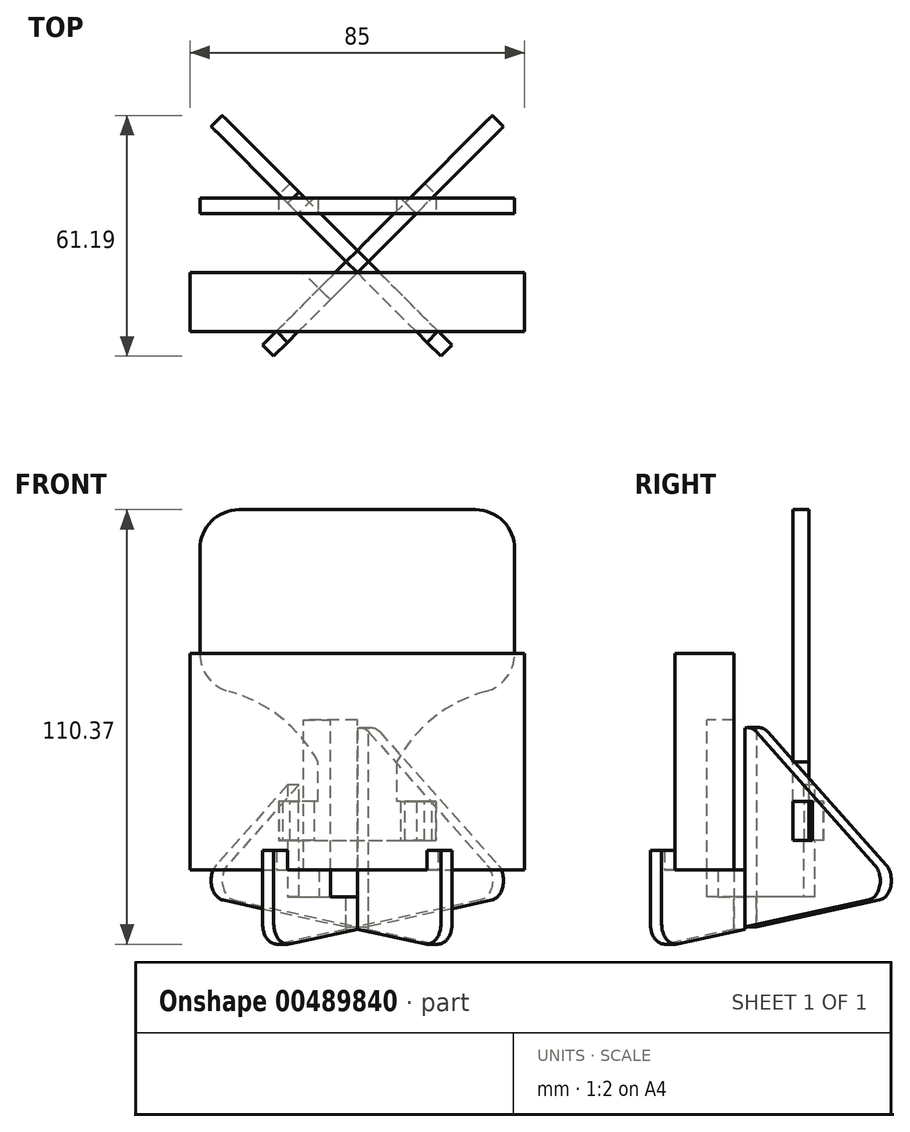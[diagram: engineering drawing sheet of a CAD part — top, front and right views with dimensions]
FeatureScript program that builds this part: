
annotation { "Feature Type Name" : "Feature", "Feature Type Description" : "" }
export const myFeature = defineFeature(function(context is Context, id is Id, definition is map)
    precondition{}
    {
        {
            var Q0;
            Q0=qCreatedBy(makeId("Front.planeOp"),FACE);
            var sketch = newSketch(context, id + "F0", { "sketchPlane" : qUnion([Q0])});
            skLineSegment(sketch, "E0.bottom", {"start": v(-42.5, 27.5) * mm, "end": v(42.5, 27.5) * mm});
            skLineSegment(sketch, "E0.top", {"start": v(-42.5, -27.5) * mm, "end": v(42.5, -27.5) * mm});
            skLineSegment(sketch, "E0.left", {"start": v(-42.5, 27.5) * mm, "end": v(-42.5, -27.5) * mm});
            skLineSegment(sketch, "E0.right", {"start": v(42.5, 27.5) * mm, "end": v(42.5, -27.5) * mm});
            skPoint(sketch, "E0.middle", {"position": v(0, 0) * mm});
            skSolve(sketch);
        }
        {
            var Q0;
            Q0=makeQuery(id+"F0.imprint","IMPRINT",FACE,{"disambiguationData":[TD([[makeQuery(id+"F0.imprint","IMPRINT",EDGE,{"derivedFrom":sQuery(id+"F0.wireOp",EDGE,"E0.bottom")}),-1.0]])]});
            extrude(context, id + "F1", {"entities" : qUnion([Q0]), "depth" : 15 * mm});
        }
        {
            var Q0;
            Q0=makeQuery(id+"F1.opExtrude","CAP_FACE",FACE,{"disambiguationData":[OSD([sQuery(id+"F0.wireOp",EDGE,"E0.bottom"),sQuery(id+"F0.wireOp",EDGE,"E0.top"),sQuery(id+"F0.wireOp",EDGE,"E0.left"),sQuery(id+"F0.wireOp",EDGE,"E0.right")])],"isStart":true});
            var sketch = newSketch(context, id + "F2", { "sketchPlane" : qUnion([Q0])});
            skLineSegment(sketch, "E1", {"start": v(0, -27.5) * mm, "end": v(0, 27.5) * mm});
            skSolve(sketch);
        }
        {
            var Q0;
            Q0=qCreatedBy(makeId("Front.planeOp"),FACE);
            var Q1;
            Q1=sQuery(id+"F2.wireOp",EDGE,"E1");
            cPlane(context, id + "F3", {"entities" : qUnion([Q0, Q1]), "cplaneType" : CPlaneType.LINE_ANGLE, "offset" : 25 * mm, "angle" : 45 * degree, "width" : 150 * mm, "height" : 150 * mm});
        }
        {
            var Q0;
            Q0=qCreatedBy(id+"F3.planeOp",FACE);
            var sketch = newSketch(context, id + "F4", { "sketchPlane" : qUnion([Q0])});
            skLineSegment(sketch, "E2", {"start": v(0, -27.5) * mm, "end": v(0, 3.7) * mm});
            skLineSegment(sketch, "E3", {"start": v(-8.11, 7.62) * mm, "end": v(-50.65, -26.24) * mm});
            skLineSegment(sketch, "E4", {"start": v(-48.3, -35.1) * mm, "end": v(24.24, -46.24) * mm});
            skLineSegment(sketch, "E5", {"start": v(30, -22.5) * mm, "end": v(25, -22.5) * mm});
            skLineSegment(sketch, "E6", {"start": v(25, -22.5) * mm, "end": v(25, -27.5) * mm});
            skLineSegment(sketch, "E7", {"start": v(25, -27.5) * mm, "end": v(0, -27.5) * mm});
            skLineSegment(sketch, "E8", {"start": v(30, -22.5) * mm, "end": v(30, -41.3) * mm});
            skPoint(sketch, "E9.visualSharp", {"position": v(0, 14.08) * mm});
            skArc(sketch, "E9.filletArc", {"start": v(0, 3.7) * mm, "mid": v(-2.83, 8.21) * mm, "end": v(-8.11, 7.62) * mm});
            skPoint(sketch, "E10.visualSharp", {"position": v(-59.6, -33.35) * mm});
            skArc(sketch, "E10.filletArc", {"start": v(-50.65, -26.24) * mm, "mid": v(-52.37, -31.43) * mm, "end": v(-48.3, -35.1) * mm});
            skPoint(sketch, "E11.visualSharp", {"position": v(30, -47.13) * mm});
            skArc(sketch, "E11.filletArc", {"start": v(24.24, -46.24) * mm, "mid": v(28.26, -45.1) * mm, "end": v(30, -41.3) * mm});
            skSolve(sketch);
        }
        {
            var Q0;
            Q0=makeQuery(id+"F4.imprint","IMPRINT",FACE,{"disambiguationData":[TD([[makeQuery(id+"F4.imprint","IMPRINT",EDGE,{"derivedFrom":sQuery(id+"F4.wireOp",EDGE,"E2")}),1.0]])]});
            extrude(context, id + "F5", {"entities" : qUnion([Q0]), "depth" : 4 * mm});
        }
        {
            var Q0;
            Q0=makeQuery(id+"F5.opExtrude","SWEPT_BODY",BODY,{"disambiguationData":[OSD([sQuery(id+"F4.wireOp",EDGE,"E2"),sQuery(id+"F4.wireOp",EDGE,"E3"),sQuery(id+"F4.wireOp",EDGE,"E4"),sQuery(id+"F4.wireOp",EDGE,"E5"),sQuery(id+"F4.wireOp",EDGE,"E6"),sQuery(id+"F4.wireOp",EDGE,"E7"),sQuery(id+"F4.wireOp",EDGE,"E8"),sQuery(id+"F4.wireOp",EDGE,"E9.filletArc"),sQuery(id+"F4.wireOp",EDGE,"E10.filletArc"),sQuery(id+"F4.wireOp",EDGE,"E11.filletArc")])]});
            var Q1;
            Q1=qCreatedBy(makeId("Right.planeOp"),FACE);
            mirror(context, id + "F6", {"entities" : qUnion([Q0]), "mirrorPlane" : qUnion([Q1])});
        }
        {
            var Q0;
            Q0=makeQuery(id+"F5.opExtrude","CAP_FACE",FACE,{"disambiguationData":[OSD([sQuery(id+"F4.wireOp",EDGE,"E2"),sQuery(id+"F4.wireOp",EDGE,"E3"),sQuery(id+"F4.wireOp",EDGE,"E4"),sQuery(id+"F4.wireOp",EDGE,"E5"),sQuery(id+"F4.wireOp",EDGE,"E6"),sQuery(id+"F4.wireOp",EDGE,"E7"),sQuery(id+"F4.wireOp",EDGE,"E8"),sQuery(id+"F4.wireOp",EDGE,"E9.filletArc"),sQuery(id+"F4.wireOp",EDGE,"E10.filletArc"),sQuery(id+"F4.wireOp",EDGE,"E11.filletArc")])],"isStart":true});
            var sketch = newSketch(context, id + "F7", { "sketchPlane" : qUnion([Q0])});
            skLineSegment(sketch, "E12.bottom", {"start": v(4, -34.3) * mm, "end": v(-9.7, -34.3) * mm});
            skLineSegment(sketch, "E12.top", {"start": v(4, 10.7) * mm, "end": v(-9.7, 10.7) * mm});
            skLineSegment(sketch, "E12.left", {"start": v(4, -34.3) * mm, "end": v(4, 10.7) * mm});
            skLineSegment(sketch, "E12.right", {"start": v(-9.7, -34.3) * mm, "end": v(-9.7, 10.7) * mm});
            skSolve(sketch);
        }
        {
            var Q0;
            Q0 = qSketchRegion(id + "F7", true);
            extrude(context, id + "F8", {"entities" : qUnion([Q0]), "operationType" : NewBodyOperationType.REMOVE, "oppositeDirection" : true, "depth" : 25 * mm});
        }
        {
            var Q0;
            Q0=makeQuery(id+"F6.opPattern","COPY",FACE,{"derivedFrom":makeQuery(id+"F5.opExtrude","CAP_FACE",FACE,{"disambiguationData":[OSD([sQuery(id+"F4.wireOp",EDGE,"E2"),sQuery(id+"F4.wireOp",EDGE,"E3"),sQuery(id+"F4.wireOp",EDGE,"E4"),sQuery(id+"F4.wireOp",EDGE,"E5"),sQuery(id+"F4.wireOp",EDGE,"E6"),sQuery(id+"F4.wireOp",EDGE,"E7"),sQuery(id+"F4.wireOp",EDGE,"E8"),sQuery(id+"F4.wireOp",EDGE,"E9.filletArc"),sQuery(id+"F4.wireOp",EDGE,"E10.filletArc"),sQuery(id+"F4.wireOp",EDGE,"E11.filletArc")])],"isStart":false}),"instanceName":"1"});
            var sketch = newSketch(context, id + "F9", { "sketchPlane" : qUnion([Q0])});
            skLineSegment(sketch, "E13.bottom", {"start": v(0, -50.3) * mm, "end": v(4, -50.3) * mm});
            skLineSegment(sketch, "E13.top", {"start": v(0, -48.84) * mm, "end": v(4, -48.84) * mm});
            skLineSegment(sketch, "E13.left", {"start": v(0, -48.84) * mm, "end": v(0, -50.3) * mm});
            skLineSegment(sketch, "E13.right", {"start": v(4, -48.84) * mm, "end": v(4, -50.3) * mm});
            skSolve(sketch);
        }
        {
            var Q0;
            Q0 = qSketchRegion(id + "F9", true);
            extrude(context, id + "F10", {"entities" : qUnion([Q0]), "operationType" : NewBodyOperationType.REMOVE, "oppositeDirection" : true, "depth" : 25 * mm});
        }
        {
            var Q0;
            Q0=makeQuery(id+"F6.opPattern","COPY",FACE,{"derivedFrom":makeQuery(id+"F5.opExtrude","CAP_FACE",FACE,{"disambiguationData":[OSD([sQuery(id+"F4.wireOp",EDGE,"E2"),sQuery(id+"F4.wireOp",EDGE,"E3"),sQuery(id+"F4.wireOp",EDGE,"E4"),sQuery(id+"F4.wireOp",EDGE,"E5"),sQuery(id+"F4.wireOp",EDGE,"E6"),sQuery(id+"F4.wireOp",EDGE,"E7"),sQuery(id+"F4.wireOp",EDGE,"E8"),sQuery(id+"F4.wireOp",EDGE,"E9.filletArc"),sQuery(id+"F4.wireOp",EDGE,"E10.filletArc"),sQuery(id+"F4.wireOp",EDGE,"E11.filletArc")])],"isStart":true}),"instanceName":"1"});
            var sketch = newSketch(context, id + "F11", { "sketchPlane" : qUnion([Q0])});
            skLineSegment(sketch, "E14.bottom", {"start": v(-4, -46.51) * mm, "end": v(0, -46.51) * mm});
            skLineSegment(sketch, "E14.top", {"start": v(-4, -34.3) * mm, "end": v(0, -34.3) * mm});
            skLineSegment(sketch, "E14.left", {"start": v(-4, -46.51) * mm, "end": v(-4, -34.3) * mm});
            skLineSegment(sketch, "E14.right", {"start": v(0, -46.51) * mm, "end": v(0, -34.3) * mm});
            skSolve(sketch);
        }
        {
            var Q0;
            Q0 = qSketchRegion(id + "F11", true);
            extrude(context, id + "F12", {"entities" : qUnion([Q0]), "operationType" : NewBodyOperationType.REMOVE, "oppositeDirection" : true, "depth" : 4 * mm});
        }
        {
            var Q0;
            Q0=qCreatedBy(makeId("Front.planeOp"),FACE);
            cPlane(context, id + "F13", {"entities" : qUnion([Q0]), "cplaneType" : CPlaneType.OFFSET, "offset" : 15 * mm, "oppositeDirection" : true, "width" : 150 * mm, "height" : 150 * mm});
        }
        {
            var Q0;
            Q0=qCreatedBy(id+"F13.planeOp",FACE);
            var sketch = newSketch(context, id + "F14", { "sketchPlane" : qUnion([Q0])});
            skLineSegment(sketch, "E15.bottom", {"start": v(-40, 64.07) * mm, "end": v(40, 64.07) * mm});
            skLineSegment(sketch, "E15.left", {"start": v(-40, 64.07) * mm, "end": v(-40, 19.07) * mm});
            skLineSegment(sketch, "E15.right", {"start": v(40, 64.07) * mm, "end": v(40, 19.07) * mm});
            skPoint(sketch, "E15.middle", {"position": v(0, 41.57) * mm});
            skArc(sketch, "E16", {"start": v(-10, 0) * mm, "mid": v(-22.5, 13.45) * mm, "end": v(-40, 19.07) * mm});
            skArc(sketch, "E17.MirrorCS", {"start": v(10, 0) * mm, "mid": v(22.5, 13.45) * mm, "end": v(40, 19.07) * mm});
            skLineSegment(sketch, "E18", {"start": v(10, 0) * mm, "end": v(10, -10) * mm});
            skLineSegment(sketch, "E19", {"start": v(10, -20) * mm, "end": v(-10, -20) * mm});
            skLineSegment(sketch, "E20", {"start": v(-10, -10) * mm, "end": v(-10, 0) * mm});
            skLineSegment(sketch, "E21", {"start": v(10, -20) * mm, "end": v(20, -20) * mm});
            skLineSegment(sketch, "E22", {"start": v(20, -20) * mm, "end": v(20, -10) * mm});
            skLineSegment(sketch, "E23", {"start": v(20, -10) * mm, "end": v(10, -10) * mm});
            skLineSegment(sketch, "E24", {"start": v(-20, -10) * mm, "end": v(-20, -20) * mm});
            skLineSegment(sketch, "E25", {"start": v(-20, -20) * mm, "end": v(-10, -20) * mm});
            skLineSegment(sketch, "E26.trimOffspring", {"start": v(-10, -10) * mm, "end": v(-20, -10) * mm});
            skSolve(sketch);
        }
        {
            var Q0;
            Q0 = qSketchRegion(id + "F14", true);
            extrude(context, id + "F15", {"entities" : qUnion([Q0]), "oppositeDirection" : true, "depth" : 4 * mm});
        }
        {
            var Q0;
            Q0=makeQuery(id+"F6.opPattern","COPY",FACE,{"derivedFrom":makeQuery(id+"F5.opExtrude","CAP_FACE",FACE,{"disambiguationData":[OSD([sQuery(id+"F4.wireOp",EDGE,"E2"),sQuery(id+"F4.wireOp",EDGE,"E3"),sQuery(id+"F4.wireOp",EDGE,"E4"),sQuery(id+"F4.wireOp",EDGE,"E5"),sQuery(id+"F4.wireOp",EDGE,"E6"),sQuery(id+"F4.wireOp",EDGE,"E7"),sQuery(id+"F4.wireOp",EDGE,"E8"),sQuery(id+"F4.wireOp",EDGE,"E9.filletArc"),sQuery(id+"F4.wireOp",EDGE,"E10.filletArc"),sQuery(id+"F4.wireOp",EDGE,"E11.filletArc")])],"isStart":true}),"instanceName":"1"});
            var sketch = newSketch(context, id + "F16", { "sketchPlane" : qUnion([Q0])});
            skLineSegment(sketch, "E27.bottom", {"start": v(-21.21, -10) * mm, "end": v(-28.08, -10) * mm});
            skLineSegment(sketch, "E27.top", {"start": v(-21.21, -20) * mm, "end": v(-28.08, -20) * mm});
            skLineSegment(sketch, "E27.left", {"start": v(-21.21, -10) * mm, "end": v(-21.21, -20) * mm});
            skLineSegment(sketch, "E27.right", {"start": v(-28.08, -10) * mm, "end": v(-28.08, -20) * mm});
            skSolve(sketch);
        }
        {
            var Q0;
            Q0 = qSketchRegion(id + "F16", true);
            extrude(context, id + "F17", {"entities" : qUnion([Q0]), "operationType" : NewBodyOperationType.REMOVE, "oppositeDirection" : true, "depth" : 25 * mm});
        }
        {
            var Q0;
            Q0=makeQuery(id+"F5.opExtrude","CAP_FACE",FACE,{"disambiguationData":[OSD([sQuery(id+"F4.wireOp",EDGE,"E2"),sQuery(id+"F4.wireOp",EDGE,"E3"),sQuery(id+"F4.wireOp",EDGE,"E4"),sQuery(id+"F4.wireOp",EDGE,"E5"),sQuery(id+"F4.wireOp",EDGE,"E6"),sQuery(id+"F4.wireOp",EDGE,"E7"),sQuery(id+"F4.wireOp",EDGE,"E8"),sQuery(id+"F4.wireOp",EDGE,"E9.filletArc"),sQuery(id+"F4.wireOp",EDGE,"E10.filletArc"),sQuery(id+"F4.wireOp",EDGE,"E11.filletArc")])],"isStart":true});
            var sketch = newSketch(context, id + "F18", { "sketchPlane" : qUnion([Q0])});
            skLineSegment(sketch, "E28.bottom", {"start": v(21.21, -10) * mm, "end": v(28.21, -10) * mm});
            skLineSegment(sketch, "E28.top", {"start": v(21.21, -20) * mm, "end": v(28.21, -20) * mm});
            skLineSegment(sketch, "E28.left", {"start": v(21.21, -10) * mm, "end": v(21.21, -20) * mm});
            skLineSegment(sketch, "E28.right", {"start": v(28.21, -10) * mm, "end": v(28.21, -20) * mm});
            skSolve(sketch);
        }
        {
            var Q0;
            Q0 = qSketchRegion(id + "F18", true);
            extrude(context, id + "F19", {"entities" : qUnion([Q0]), "operationType" : NewBodyOperationType.REMOVE, "oppositeDirection" : true, "depth" : 25 * mm});
        }
        {
            var Q0;
            Q0=makeQuery(id+"F15.opExtrude","SWEPT_EDGE",EDGE,{"disambiguationData":[OSD([sQuery(id+"F14.wireOp",EDGE,"E15.bottom"),sQuery(id+"F14.wireOp",EDGE,"E15.right")])]});
            var Q1;
            Q1=makeQuery(id+"F15.opExtrude","SWEPT_EDGE",EDGE,{"disambiguationData":[OSD([sQuery(id+"F14.wireOp",EDGE,"E15.right"),sQuery(id+"F14.wireOp",EDGE,"E17.MirrorCS")])]});
            var Q2;
            Q2=makeQuery(id+"F15.opExtrude","SWEPT_EDGE",EDGE,{"disambiguationData":[OSD([sQuery(id+"F14.wireOp",EDGE,"E15.bottom"),sQuery(id+"F14.wireOp",EDGE,"E15.left")])]});
            var Q3;
            Q3=makeQuery(id+"F15.opExtrude","SWEPT_EDGE",EDGE,{"disambiguationData":[OSD([sQuery(id+"F14.wireOp",EDGE,"E15.left"),sQuery(id+"F14.wireOp",EDGE,"E16")])]});
            fillet(context, id + "F20", {"entities" : qUnion([Q0, Q1, Q2, Q3]), "radius" : 10 * mm, "tangentPropagation" : true, "allowEdgeOverflow" : false});
        }
    });
